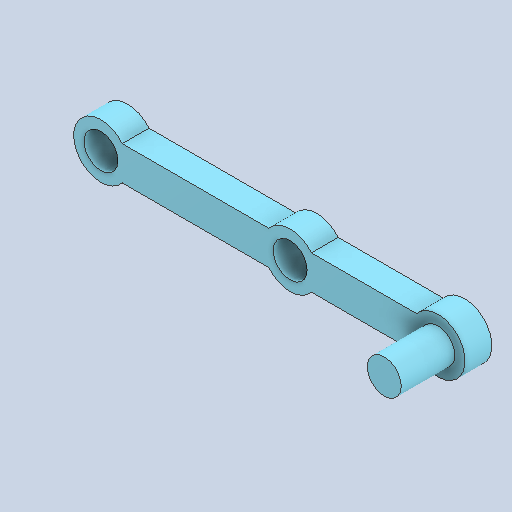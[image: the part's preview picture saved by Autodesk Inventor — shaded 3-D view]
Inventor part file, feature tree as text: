
AUTODESK INVENTOR PART (.ipt)
format: ipt  version: 2022 (Build 260153000, 153)  size: 122,880 bytes
history: native  units: in
note: dims shown in document units (in); Inventor stores cm internally (conversion verified against a paired STEP export)
features: other x3, sketch x1
ambient origin geometry x8: Origin, YZ Plane, XZ Plane, XY Plane, X Axis, Y Axis, Z Axis, Center Point
bodies: Solid1 (feature_tree)
feature tree (4):
  other  "Component38.ipt"
  other  "Solid1::Component38.ipt"
  other  "TaggingFeature1"
  sketch  "Sketch2"  dims[d0=0.3937in]
